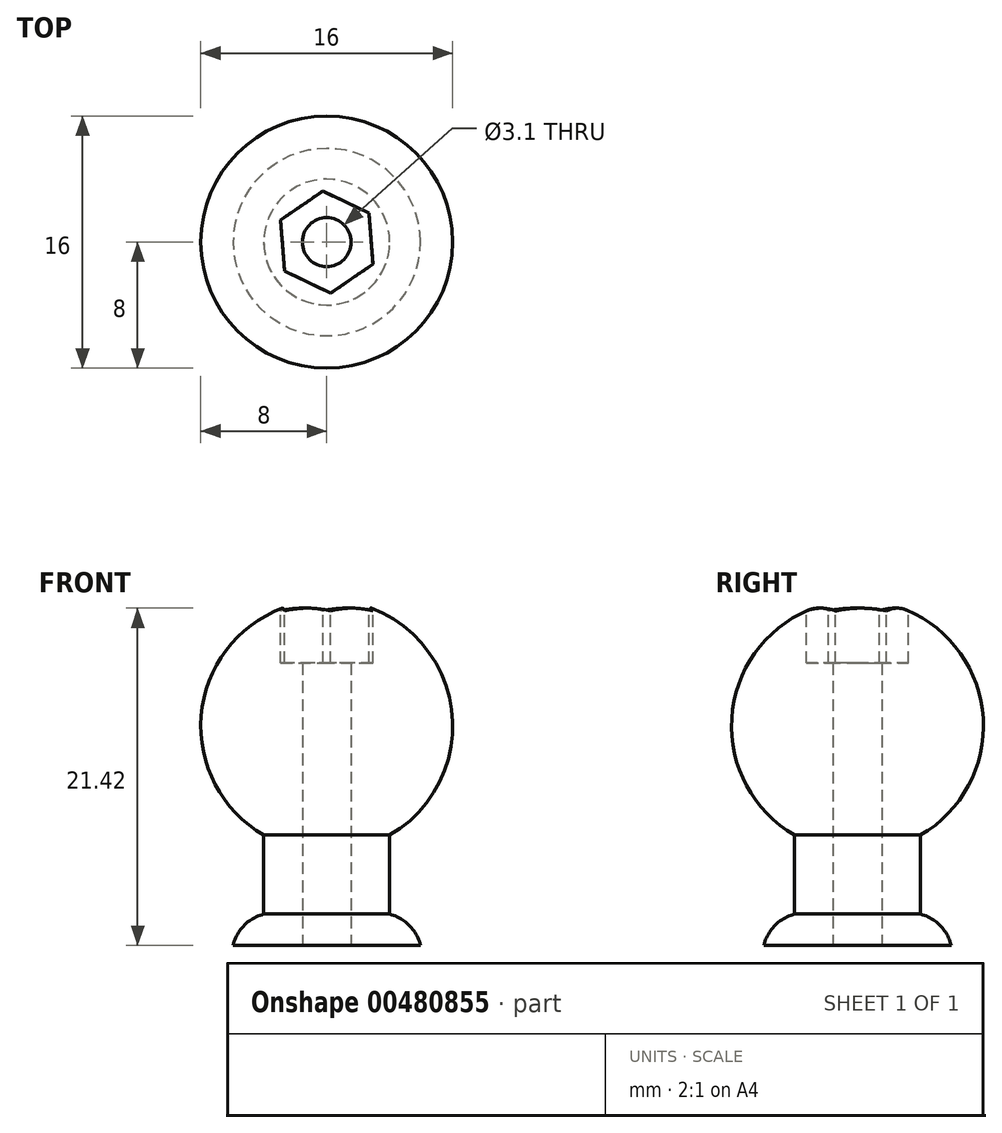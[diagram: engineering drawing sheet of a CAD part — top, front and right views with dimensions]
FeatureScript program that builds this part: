
annotation { "Feature Type Name" : "Feature", "Feature Type Description" : "" }
export const myFeature = defineFeature(function(context is Context, id is Id, definition is map)
    precondition{}
    {
        {
            var Q0;
            Q0=qCreatedBy(makeId("Front.planeOp"),FACE);
            var sketch = newSketch(context, id + "F0", { "sketchPlane" : qUnion([Q0])});
            skLineSegment(sketch, "E0", {"start": v(0, 55.43) * mm, "end": v(0, -68.75) * mm, "construction": true});
            skSolve(sketch);
        }
        {
            var Q0;
            Q0=qCreatedBy(makeId("Front.planeOp"),FACE);
            var sketch = newSketch(context, id + "F1", { "sketchPlane" : qUnion([Q0])});
            skLineSegment(sketch, "E1.top", {"start": v(-4, -13.93) * mm, "end": v(0, -13.93) * mm});
            skLineSegment(sketch, "E1.left", {"start": v(-4, -6.93) * mm, "end": v(-4, -13.93) * mm});
            skArc(sketch, "E2", {"start": v(0, 8) * mm, "mid": v(-7.73, 2.07) * mm, "end": v(-4, -6.93) * mm});
            skLineSegment(sketch, "E3", {"start": v(0, 8) * mm, "end": v(0, -13.93) * mm});
            skSolve(sketch);
        }
        {
            var Q0;
            Q0=makeQuery(id+"F1.imprint","IMPRINT",FACE,{"disambiguationData":[TD([[makeQuery(id+"F1.imprint","IMPRINT",EDGE,{"derivedFrom":sQuery(id+"F1.wireOp",EDGE,"E1.top")}),1.0]])]});
            var Q1;
            Q1=sQuery(id+"F0.wireOp",EDGE,"E0");
            revolve(context, id + "F2", {"entities" : qUnion([Q0]), "axis" : qUnion([Q1]), "revolveType" : RevolveType.FULL});
        }
        {
            var Q0;
            Q0=makeQuery(id+"F2.opRevolve","SWEPT_FACE",FACE,{"disambiguationData":[OSD([sQuery(id+"F1.wireOp",EDGE,"E1.top")])]});
            var sketch = newSketch(context, id + "F3", { "sketchPlane" : qUnion([Q0])});
            skCircle(sketch, "E4", {"center": v(0, 0) * mm, "radius": 1.55 * mm});
            skSolve(sketch);
        }
        {
            var Q0;
            Q0=qSketchRegion(id+"F3",true);
            var Q1;
            Q1=qSketchRegion(id+"F0",true);
            extrude(context, id + "F4", {"entities" : qUnion([Q0, Q1]), "operationType" : NewBodyOperationType.REMOVE, "endBound" : BoundingType.UP_TO_NEXT, "oppositeDirection" : true, "depth" : 50 * mm});
        }
        {
            var Q0;
            Q0=qCreatedBy(makeId("Top.planeOp"),FACE);
            cPlane(context, id + "F5", {"entities" : qUnion([Q0]), "cplaneType" : CPlaneType.OFFSET, "offset" : 8 * mm, "width" : 150 * mm, "height" : 150 * mm});
        }
        {
            var Q0;
            Q0=qCreatedBy(id+"F5.planeOp",FACE);
            var sketch = newSketch(context, id + "F6", { "sketchPlane" : qUnion([Q0])});
            skCircle(sketch, "E5.cCircle", {"center": v(0, 0) * mm, "radius": 3.25 * mm, "construction": true});
            skLineSegment(sketch, "E5.0", {"start": v(2.93, -1.4) * mm, "end": v(0.25, -3.24) * mm});
            skLineSegment(sketch, "E5.1", {"start": v(0.25, -3.24) * mm, "end": v(-2.68, -1.84) * mm});
            skLineSegment(sketch, "E5.2", {"start": v(-2.68, -1.84) * mm, "end": v(-2.93, 1.4) * mm});
            skLineSegment(sketch, "E5.3", {"start": v(-2.93, 1.4) * mm, "end": v(-0.25, 3.24) * mm});
            skLineSegment(sketch, "E5.4", {"start": v(-0.25, 3.24) * mm, "end": v(2.68, 1.84) * mm});
            skLineSegment(sketch, "E5.5", {"start": v(2.68, 1.84) * mm, "end": v(2.93, -1.4) * mm});
            skSolve(sketch);
        }
        {
            var Q0;
            Q0=makeQuery(id+"F6.imprint","IMPRINT",FACE,{"disambiguationData":[TD([[makeQuery(id+"F6.imprint","IMPRINT",EDGE,{"derivedFrom":sQuery(id+"F6.wireOp",EDGE,"E5.0")}),-1.0]])]});
            extrude(context, id + "F7", {"entities" : qUnion([Q0]), "operationType" : NewBodyOperationType.REMOVE, "oppositeDirection" : true, "depth" : 4 * mm});
        }
        {
            var Q0;
            Q0=qCreatedBy(makeId("Front.planeOp"),FACE);
            var sketch = newSketch(context, id + "F8", { "sketchPlane" : qUnion([Q0])});
            skLineSegment(sketch, "E6", {"start": v(3.95, -13.93) * mm, "end": v(5.95, -13.93) * mm});
            skLineSegment(sketch, "E7", {"start": v(3.93, -11.93) * mm, "end": v(3.95, -13.93) * mm});
            skArc(sketch, "E8", {"start": v(5.95, -13.93) * mm, "mid": v(5.23, -12.64) * mm, "end": v(3.93, -11.93) * mm});
            skSolve(sketch);
        }
        {
            var Q0;
            Q0=qSketchRegion(id+"F8",true);
            var Q1;
            Q1=sQuery(id+"F0.wireOp",EDGE,"E0");
            revolve(context, id + "F9", {"operationType" : NewBodyOperationType.ADD, "entities" : qUnion([Q0]), "axis" : qUnion([Q1]), "revolveType" : RevolveType.FULL, "surfaceOperationType" : NewSurfaceOperationType.NEW});
        }
    });
